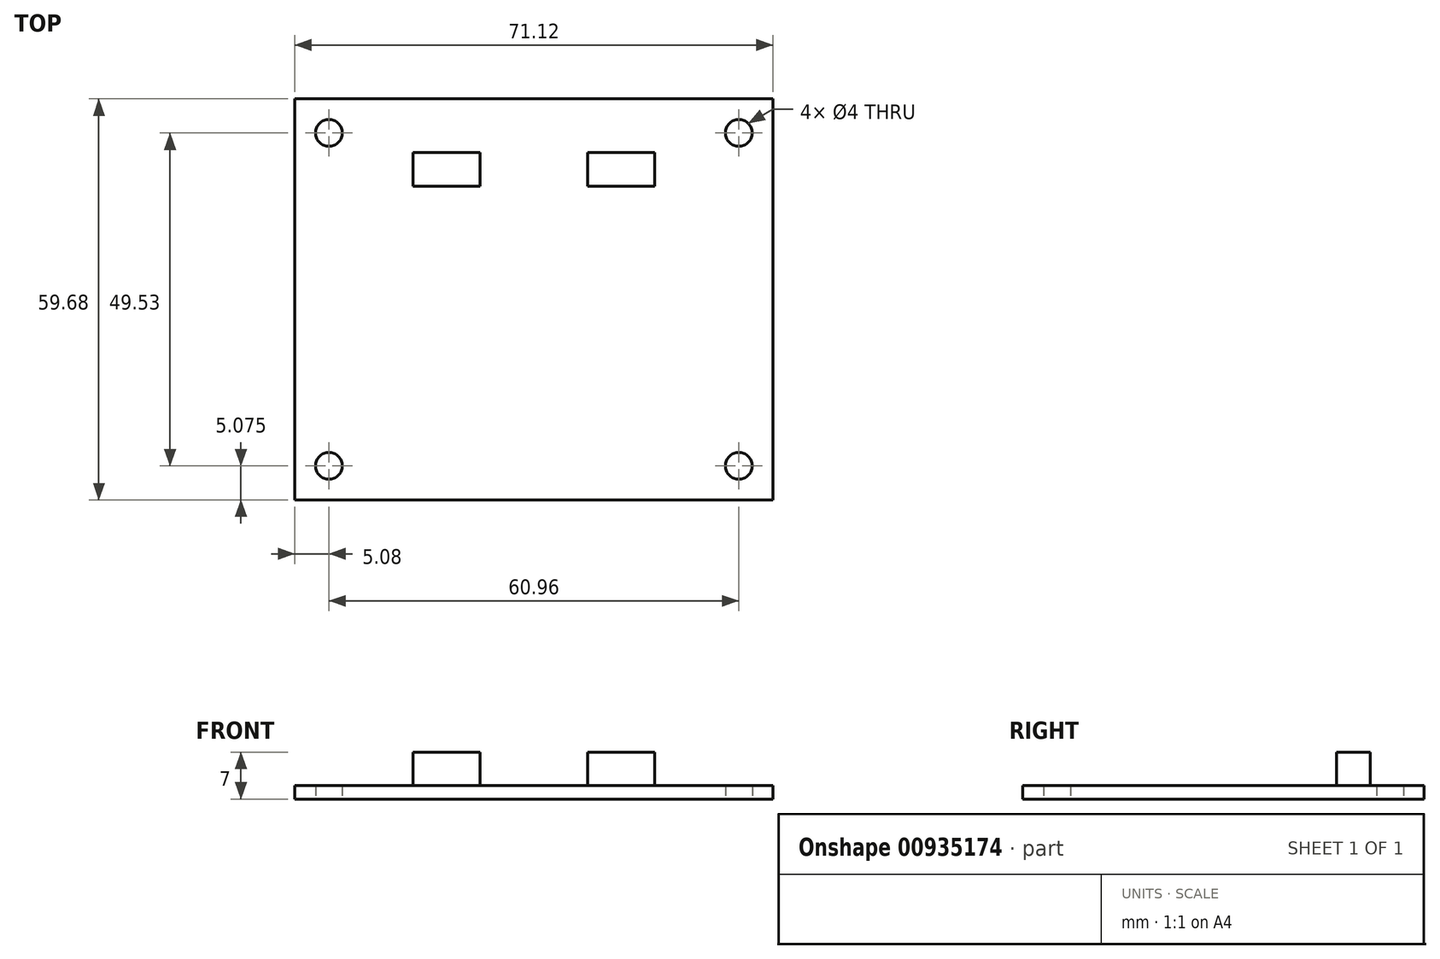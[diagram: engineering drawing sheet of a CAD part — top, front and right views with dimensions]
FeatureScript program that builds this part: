
annotation { "Feature Type Name" : "Feature", "Feature Type Description" : "" }
export const myFeature = defineFeature(function(context is Context, id is Id, definition is map)
    precondition{}
    {
        {
            var Q0;
            Q0=qCreatedBy(makeId("Top.planeOp"),FACE);
            var sketch = newSketch(context, id + "F0", { "sketchPlane" : qUnion([Q0])});
            skLineSegment(sketch, "E0.bottom", {"start": v(-35.56, 29.85) * mm, "end": v(35.56, 29.85) * mm});
            skLineSegment(sketch, "E0.top", {"start": v(-35.56, -29.85) * mm, "end": v(35.56, -29.85) * mm});
            skLineSegment(sketch, "E0.left", {"start": v(-35.56, 29.85) * mm, "end": v(-35.56, -29.84) * mm});
            skLineSegment(sketch, "E0.right", {"start": v(35.56, 29.85) * mm, "end": v(35.56, -29.85) * mm});
            skPoint(sketch, "E0.middle", {"position": v(0, 0) * mm});
            skCircle(sketch, "E1", {"center": v(-30.48, 24.77) * mm, "radius": 2 * mm});
            skCircle(sketch, "E2.MirrorC", {"center": v(30.48, 24.77) * mm, "radius": 2 * mm});
            skCircle(sketch, "E3.MirrorC", {"center": v(-30.48, -24.77) * mm, "radius": 2 * mm});
            skCircle(sketch, "E4.MirrorC", {"center": v(30.48, -24.76) * mm, "radius": 2 * mm});
            skSolve(sketch);
        }
        {
            var Q0;
            Q0=qSketchRegion(id+"F0",true);
            extrude(context, id + "F1", {"entities" : qUnion([Q0]), "depth" : 2 * mm, "offsetDistance" : 25 * mm});
        }
        {
            var Q0;
            Q0=makeQuery(id+"F1.opExtrude","CAP_FACE",FACE,{"disambiguationData":[OSD([sQuery(id+"F0.wireOp",EDGE,"E0.bottom"),sQuery(id+"F0.wireOp",EDGE,"E0.top"),sQuery(id+"F0.wireOp",EDGE,"E0.left"),sQuery(id+"F0.wireOp",EDGE,"E0.right"),sQuery(id+"F0.wireOp",EDGE,"E1"),sQuery(id+"F0.wireOp",EDGE,"E2.MirrorC"),sQuery(id+"F0.wireOp",EDGE,"E3.MirrorC"),sQuery(id+"F0.wireOp",EDGE,"E4.MirrorC")])],"isStart":false});
            var sketch = newSketch(context, id + "F2", { "sketchPlane" : qUnion([Q0])});
            skLineSegment(sketch, "E5.bottom", {"start": v(-18, 16.85) * mm, "end": v(-8, 16.85) * mm});
            skLineSegment(sketch, "E5.top", {"start": v(-18, 21.85) * mm, "end": v(-8, 21.85) * mm});
            skLineSegment(sketch, "E5.left", {"start": v(-18, 16.85) * mm, "end": v(-18, 21.85) * mm});
            skLineSegment(sketch, "E5.right", {"start": v(-8, 16.85) * mm, "end": v(-8, 21.85) * mm});
            skLineSegment(sketch, "E6.MirrorCS", {"start": v(18, 16.85) * mm, "end": v(8, 16.85) * mm});
            skLineSegment(sketch, "E7.MirrorCS", {"start": v(18, 21.85) * mm, "end": v(8, 21.85) * mm});
            skLineSegment(sketch, "E8.MirrorCS", {"start": v(18, 16.85) * mm, "end": v(18, 21.85) * mm});
            skLineSegment(sketch, "E9.MirrorCS", {"start": v(8, 16.85) * mm, "end": v(8, 21.85) * mm});
            skSolve(sketch);
        }
        {
            var Q0;
            Q0=qSketchRegion(id+"F2",true);
            extrude(context, id + "F3", {"entities" : qUnion([Q0]), "depth" : 5 * mm, "offsetDistance" : 25 * mm});
        }
    });
